# Revit family: Storage-Freestanding-Teknion-B_STR_Top for Solid-R2019
name_source: partatom
category: Furniture
units: mm (PartAtom-declared; Revit-internal decimal feet)

## family parameters
Always vertical = Yes
Cut with Voids When Loaded = No
OmniClass Number = 23.40.70.14.64.21
OmniClass Title = Systems Furniture
Room Calculation Point = No
Shared = Yes
Work Plane-Based = Yes

## types (3) — shared parameters
Assembly Code = E2020200
Default Elevation = 48 "
Manufacturer = Teknion
Manufacturer Fax = 416.661.4586
Part Number = B_STR
Product Documentation Link = http://www.teknion.com
Product Line = Expansion Casegoods
Product Page URL = https://www.teknion.com
Series = Expansion Casegoods
Sustainability Data = http://www.teknion.com
URL = http://www.teknion.com
Unit Weight URL = http://www.teknion.com
Warranty = https://www.teknion.com

## per-type parameters (varying)
| type | 1" WS | 1-3/16" WS | 1-9/16" WS | Description | Model | Worksurface Thickness |
| 1" Thick WS | Yes | No | No | Top for Solid Storage (1" Thick Worksurface) | BDSTR____ | 1.016 " |
| 1-3/6" Thick WS | No | Yes | No | Top for Solid Storage (1-3/16" Thick Worksurface) | BMSTR____ | 1.189 " |
| 1-9/16" Thick WS | No | No | Yes | Top for Solid Storage (1-9/16" Thick Worksurface) | BXSTR____ | 1.555 " |

## geometry (parser evidence)
native form markers: Blend x2, Sweep x2
no freeform markers — native parametric forms only
